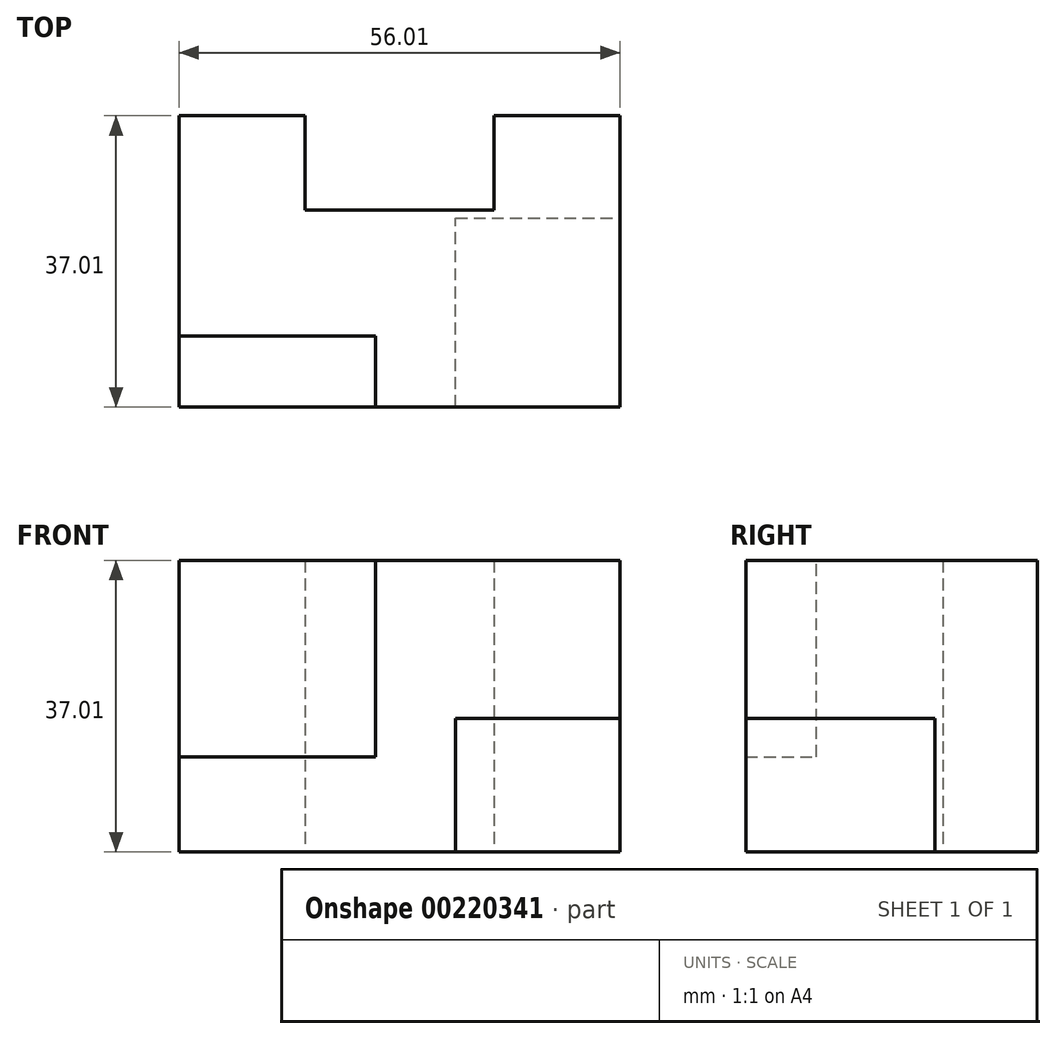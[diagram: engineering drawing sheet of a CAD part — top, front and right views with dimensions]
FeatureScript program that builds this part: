
annotation { "Feature Type Name" : "Feature", "Feature Type Description" : "" }
export const myFeature = defineFeature(function(context is Context, id is Id, definition is map)
    precondition{}
    {
        {
            var Q0;
            Q0=qCreatedBy(makeId("Top.planeOp"),FACE);
            var sketch = newSketch(context, id + "F0", { "sketchPlane" : qUnion([Q0])});
            skLineSegment(sketch, "E0.bottom", {"start": v(0, 0) * mm, "end": v(56, 0) * mm});
            skLineSegment(sketch, "E0.top", {"start": v(0, 37) * mm, "end": v(16, 37) * mm});
            skLineSegment(sketch, "E0.left", {"start": v(0, 0) * mm, "end": v(0, 37) * mm});
            skLineSegment(sketch, "E0.right", {"start": v(56, 0) * mm, "end": v(56, 37) * mm});
            skLineSegment(sketch, "E1.0", {"start": v(16, 25.02) * mm, "end": v(16, 37) * mm});
            skLineSegment(sketch, "E2.0", {"start": v(40, 25.02) * mm, "end": v(40, 37) * mm});
            skLineSegment(sketch, "E3.0", {"start": v(16, 25.02) * mm, "end": v(40, 25.02) * mm});
            skLineSegment(sketch, "E4.trimOffspring", {"start": v(40, 37) * mm, "end": v(56, 37) * mm});
            skSolve(sketch);
        }
        {
            var Q0;
            Q0=makeQuery(id+"F0.imprint","IMPRINT",FACE,{"disambiguationData":[TD([[makeQuery(id+"F0.imprint","IMPRINT",EDGE,{"derivedFrom":sQuery(id+"F0.wireOp",EDGE,"E0.bottom")}),1.0]])]});
            extrude(context, id + "F1", {"entities" : qUnion([Q0]), "depth" : 37 * mm});
        }
        {
            var Q0;
            Q0=makeQuery(id+"F1.opExtrude","CAP_FACE",FACE,{"disambiguationData":[OSD([sQuery(id+"F0.wireOp",EDGE,"E0.bottom"),sQuery(id+"F0.wireOp",EDGE,"E0.top"),sQuery(id+"F0.wireOp",EDGE,"E0.left"),sQuery(id+"F0.wireOp",EDGE,"E0.right"),sQuery(id+"F0.wireOp",EDGE,"E1.0"),sQuery(id+"F0.wireOp",EDGE,"E2.0"),sQuery(id+"F0.wireOp",EDGE,"E3.0"),sQuery(id+"F0.wireOp",EDGE,"E4.trimOffspring")])],"isStart":false});
            var sketch = newSketch(context, id + "F2", { "sketchPlane" : qUnion([Q0])});
            skLineSegment(sketch, "E5.bottom", {"start": v(0, 0) * mm, "end": v(24.97, 0) * mm});
            skLineSegment(sketch, "E5.top", {"start": v(0, 9) * mm, "end": v(24.97, 9) * mm});
            skLineSegment(sketch, "E5.left", {"start": v(0, 0) * mm, "end": v(0, 9) * mm});
            skLineSegment(sketch, "E5.right", {"start": v(24.97, 0) * mm, "end": v(24.97, 9) * mm});
            skSolve(sketch);
        }
        {
            var Q0;
            Q0=makeQuery(id+"F2.imprint","IMPRINT",FACE,{"disambiguationData":[TD([[makeQuery(id+"F2.imprint","IMPRINT",EDGE,{"derivedFrom":sQuery(id+"F2.wireOp",EDGE,"E5.bottom")}),1.0]])]});
            extrude(context, id + "F3", {"entities" : qUnion([Q0]), "operationType" : NewBodyOperationType.REMOVE, "oppositeDirection" : true, "depth" : 24.94 * mm});
        }
        {
            var Q0;
            Q0=makeQuery(id+"F1.opExtrude","SWEPT_FACE",FACE,{"disambiguationData":[OSD([sQuery(id+"F0.wireOp",EDGE,"E0.right")])]});
            var sketch = newSketch(context, id + "F4", { "sketchPlane" : qUnion([Q0])});
            skLineSegment(sketch, "E6.bottom", {"start": v(0, 0) * mm, "end": v(24, 0) * mm});
            skLineSegment(sketch, "E6.top", {"start": v(0, 16.94) * mm, "end": v(24, 16.94) * mm});
            skLineSegment(sketch, "E6.left", {"start": v(0, 0) * mm, "end": v(0, 16.94) * mm});
            skLineSegment(sketch, "E6.right", {"start": v(24, 0) * mm, "end": v(24, 16.94) * mm});
            skSolve(sketch);
        }
        {
            var Q0;
            Q0=makeQuery(id+"F4.imprint","IMPRINT",FACE,{"disambiguationData":[TD([[makeQuery(id+"F4.imprint","IMPRINT",EDGE,{"derivedFrom":sQuery(id+"F4.wireOp",EDGE,"E6.bottom")}),1.0]])]});
            extrude(context, id + "F5", {"entities" : qUnion([Q0]), "operationType" : NewBodyOperationType.REMOVE, "oppositeDirection" : true, "depth" : 20.85 * mm});
        }
    });
